# Revit family: JOMA_Gerberbeslag
name_source: partatom
category: Structural Connections
revit_build: Autodesk Revit Structure 2012 (Build: 20110309_2315(x64)
units: mm (PartAtom-declared; Revit-internal decimal feet)

## types (6) — shared parameters
Länk Joma Dimensioneringsverktyg = http://www.joma.se
Material = Varmförzinkad stålplåt
b = 220 mm  [stored 0.721785 ft]
t = 2 mm  [stored 0.00656168 ft]
zero-valued in all types: Default Elevation

## per-type parameters (varying)
| type | Typ | Typ 120 | Typ 140 | Typ 160 | Typ 180 | Typ 200 | Typ 220 | Vikt | h | l |
| 5622120 | TYP 120 | Yes | No | No | No | No | No | 0,46 | 20 mm  [stored 0.0656168 ft] | 120 mm  [stored 0.393701 ft] |
| 5622140 | TYP 140 | No | Yes | No | No | No | No | 0,54 | 20 mm  [stored 0.0656168 ft] | 140 mm  [stored 0.459318 ft] |
| 5622160 | TYP 160 | No | No | Yes | No | No | No | 0,60 | 20 mm  [stored 0.0656168 ft] | 160 mm  [stored 0.524934 ft] |
| 5622180 | TYP 180 | No | No | No | Yes | No | No | 0,65 | 20 mm  [stored 0.0656168 ft] | 180 mm  [stored 0.590551 ft] |
| 5622200 | TYP 200 | No | No | No | No | Yes | No | 0,72 | 20 mm  [stored 0.0656168 ft] | 200 mm  [stored 0.656168 ft] |
| 5622220 | TYP 220 | No | No | No | No | No | Yes | 0,81 | 18 mm  [stored 0.0590551 ft] | 220 mm  [stored 0.721785 ft] |

note: [stored X ft] marks values corroborated as IEEE doubles in the binary element streams (Revit-internal decimal feet)

## geometry (parser evidence)
native form markers: Sweep x2
no freeform markers — native parametric forms only
